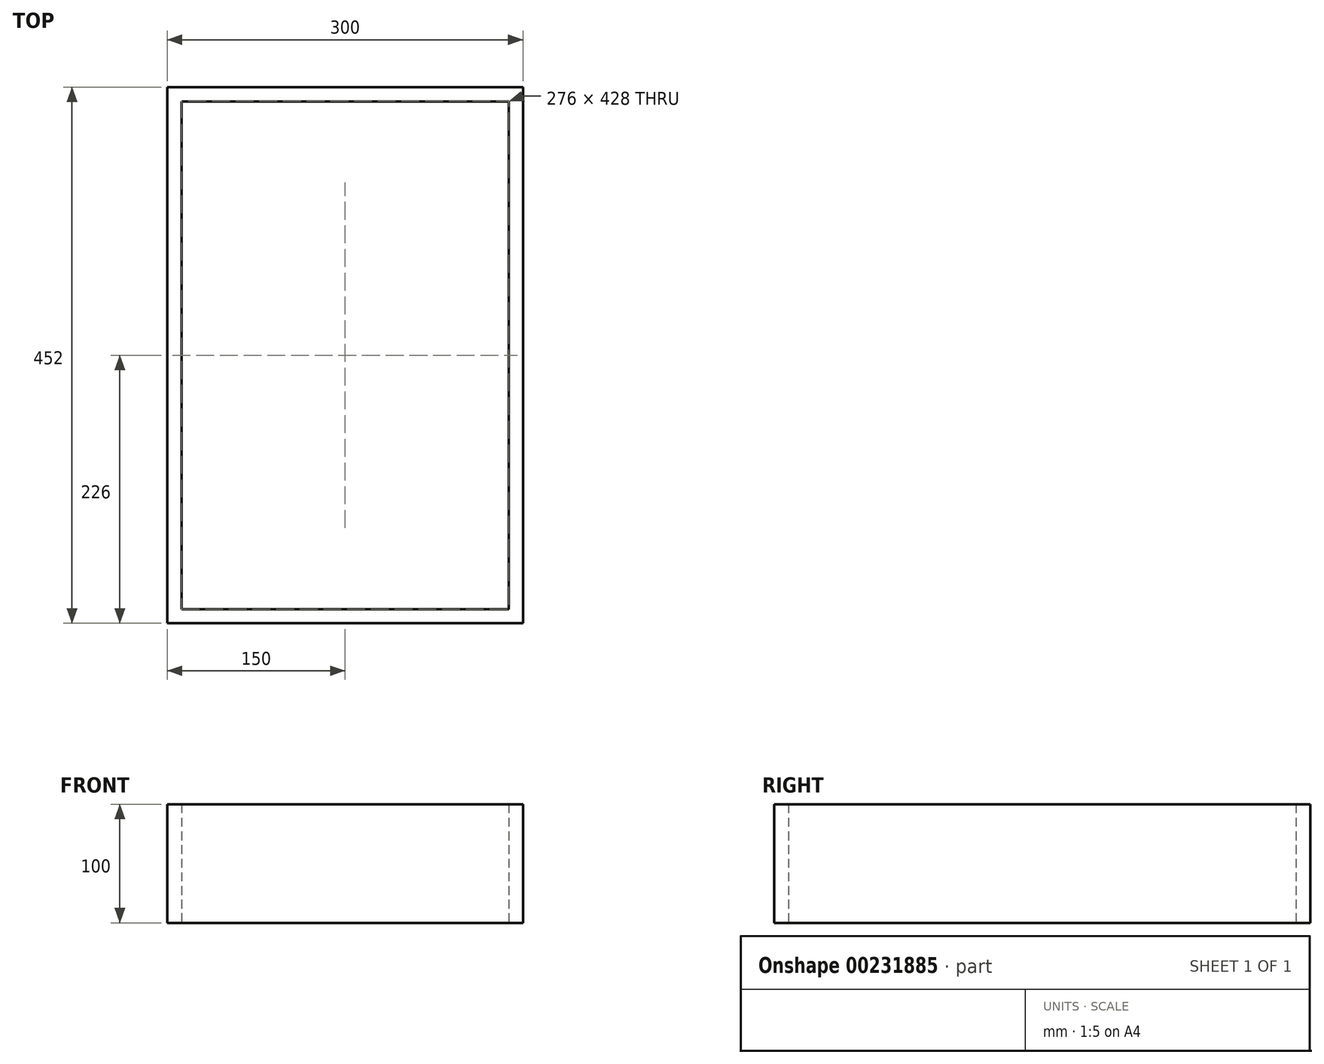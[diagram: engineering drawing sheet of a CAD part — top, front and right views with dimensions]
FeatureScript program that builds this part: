
annotation { "Feature Type Name" : "Feature", "Feature Type Description" : "" }
export const myFeature = defineFeature(function(context is Context, id is Id, definition is map)
    precondition{}
    {
        {
            var Q0;
            Q0=qCreatedBy(makeId("Top.planeOp"),FACE);
            var sketch = newSketch(context, id + "F0", { "sketchPlane" : qUnion([Q0])});
            skLineSegment(sketch, "E0.bottom", {"start": v(0, 0) * mm, "end": v(300, 0) * mm});
            skLineSegment(sketch, "E0.top", {"start": v(0, 452) * mm, "end": v(300, 452) * mm});
            skLineSegment(sketch, "E0.left", {"start": v(0, 0) * mm, "end": v(0, 452) * mm});
            skLineSegment(sketch, "E0.right", {"start": v(300, 0) * mm, "end": v(300, 452) * mm});
            skLineSegment(sketch, "E1.0", {"start": v(12, 12) * mm, "end": v(12, 440) * mm});
            skLineSegment(sketch, "E1.1", {"start": v(12, 12) * mm, "end": v(288, 12) * mm});
            skLineSegment(sketch, "E1.2", {"start": v(288, 12) * mm, "end": v(288, 440) * mm});
            skLineSegment(sketch, "E1.3", {"start": v(12, 440) * mm, "end": v(288, 440) * mm});
            skSolve(sketch);
        }
        {
            var Q0;
            Q0 = qSketchRegion(id + "F0", true);
            extrude(context, id + "F1", {"entities" : qUnion([Q0]), "depth" : 100 * mm});
        }
    });
